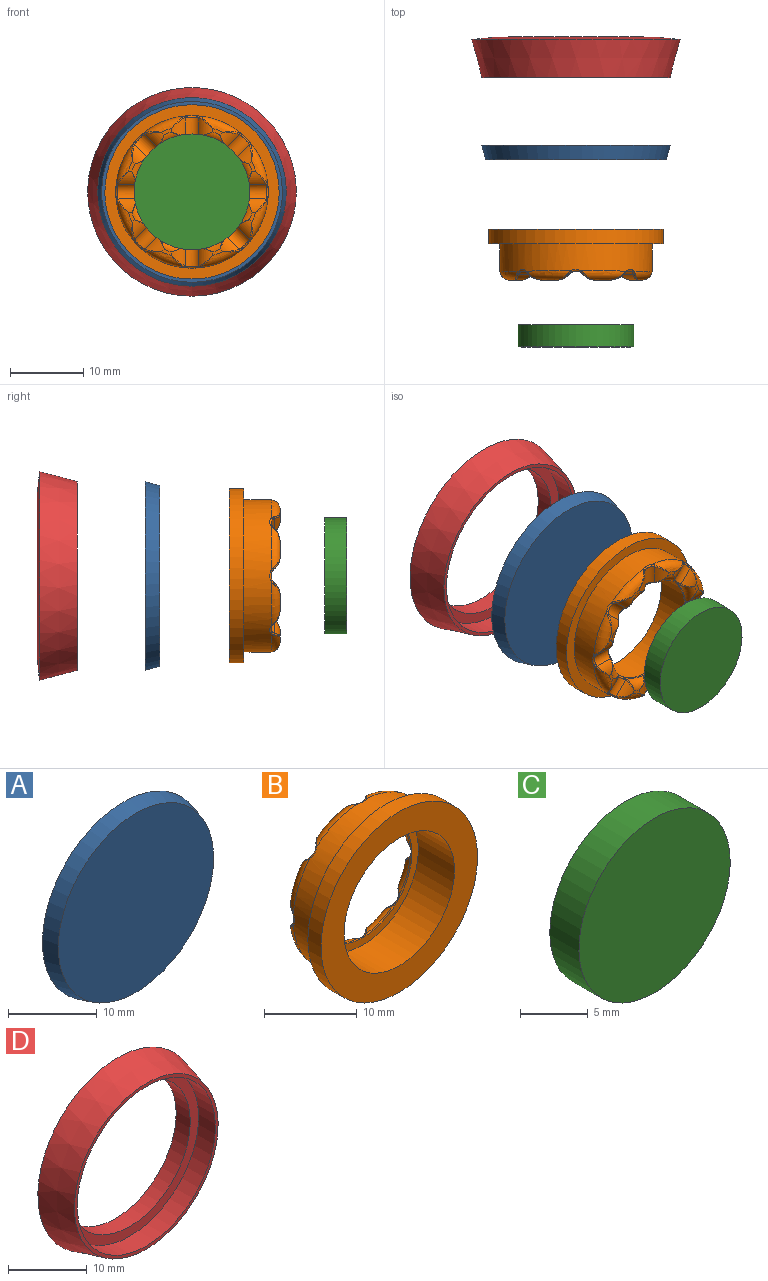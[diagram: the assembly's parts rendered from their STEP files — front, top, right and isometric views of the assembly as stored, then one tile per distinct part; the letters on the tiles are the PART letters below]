
ASSEMBLY  parts=4 mates=3
PART A: 3 faces, bbox 25.8x2x25.8 mm
  f0: plane 25.76x25.76mm, normal (0,1,0), area 521mm2, adj f1
  f1: cone r=12.35mm half-angle=14.9deg, axis (0,1,0), area 164mm2, adj f0,f2
  f2: plane 24.69x24.69mm, normal (0,-1,0), area 478.9mm2, adj f1
PART B: 135 faces, bbox 23.8x7x23.8 mm
  f0: plane 1.3x0.88mm, normal (0,1,0), area 0.6mm2, adj f3,f9,f49,f52
  f1: plane 1.3x0.88mm, normal (0,1,0), area 0.6mm2, adj f4,f10,f46,f51
  f2: plane 1.3x0.88mm, normal (0,1,0), area 0.6mm2, adj f5,f11,f33,f48
  f3: torus R=9.14mm, axis (0,-1,0), area 8.6mm2, adj f0,f29,f105,f106,f123,f124
  f4: torus R=9.14mm, axis (0,-1,0), area 8.6mm2, adj f1,f29,f95,f96,f108,f109
  f5: torus R=9.14mm, axis (0,-1,0), area 8.6mm2, adj f2,f29,f90,f91,f98,f99
  f6: torus R=9.14mm, axis (0,-1,0), area 8.6mm2, adj f15,f29,f80,f81,f93,f94
  f7: torus R=9.14mm, axis (0,-1,0), area 8.6mm2, adj f16,f29,f55,f56,f73,f74
  f8: torus R=9.14mm, axis (0,-1,0), area 8.6mm2, adj f29,f30,f70,f71,f83,f84
  f9: torus R=8.68mm, axis (0,-1,0), area 5.4mm2, adj f0,f23,f110,f111,f118,f119
  f10: torus R=8.68mm, axis (0,-1,0), area 5.4mm2, adj f1,f23,f100,f101,f113,f114
  f11: torus R=8.68mm, axis (0,-1,0), area 5.4mm2, adj f2,f23,f85,f86,f103,f104
  f12: torus R=8.68mm, axis (0,-1,0), area 5.4mm2, adj f15,f23,f75,f76,f88,f89
  f13: torus R=8.68mm, axis (0,-1,0), area 5.4mm2, adj f16,f23,f60,f61,f68,f69
  f14: torus R=8.68mm, axis (0,-1,0), area 5.4mm2, adj f23,f30,f65,f66,f78,f79
  f15: plane 1.3x0.88mm, normal (0,1,0), area 0.6mm2, adj f6,f12,f31,f43
  f16: plane 1.3x0.88mm, normal (0,1,0), area 0.6mm2, adj f7,f13,f38,f40
  f17: plane 1.3x0.88mm, normal (0,1,0), area 0.6mm2, adj f20,f22,f36,f41
  f18: plane 1.3x0.88mm, normal (0,1,0), area 0.6mm2, adj f19,f21,f34,f54
  f19: torus R=9.14mm, axis (0,-1,0), area 8.6mm2, adj f18,f29,f120,f121,f125,f126
  f20: torus R=9.14mm, axis (0,-1,0), area 8.6mm2, adj f17,f29,f58,f59,f128,f129
  f21: torus R=8.68mm, axis (0,-1,0), area 5.4mm2, adj f18,f23,f115,f116,f130,f131
  f22: torus R=8.68mm, axis (0,-1,0), area 5.4mm2, adj f17,f23,f63,f64,f133,f134
  f23: cylinder r=7.41mm len=14.83mm, axis (0,1,0), area 9.1mm2, adj f9,f10,f11,f12,f13,f14,f21,f22
  f24: plane 16.83x16.83mm, normal (0,-1,0), area 49.7mm2, adj f23,f25
  f25: cylinder r=8.41mm len=16.83mm, axis (0,1,0), area 290.8mm2, adj f24,f26
  f26: plane 23.83x23.83mm, normal (0,-1,0), area 223.5mm2, adj f25,f27
  f27: cylinder r=11.91mm len=23.83mm, axis (0,1,0), area 149.7mm2, adj f26,f28
  f28: plane 23.83x23.83mm, normal (0,1,0), area 105.2mm2, adj f27,f29
  f29: cylinder r=10.41mm len=20.83mm, axis (0,1,0), area 242.4mm2, adj f3,f4,f5,f6,f7,f8,f19,f20
  f30: plane 1.3x0.88mm, normal (0,1,0), area 0.6mm2, adj f8,f14,f37,f44
  f31: cylinder r=2.54mm len=2.53mm, axis (0,0,-1), area 3.5mm2, adj f15,f32,f89,f94
  f32: cylinder r=1.27mm len=2.61mm, axis (0,0,-1), area 5.5mm2, adj f31,f33,f86,f87,f88,f91,f92,f93
  f33: cylinder r=2.54mm len=2.53mm, axis (0,0,-1), area 3.5mm2, adj f2,f32,f85,f90
  f34: cylinder r=2.54mm len=2.53mm, axis (0,0,-1), area 3.5mm2, adj f18,f35,f125,f130
  f35: cylinder r=1.27mm len=2.61mm, axis (0,0,-1), area 5.5mm2, adj f34,f36,f126,f127,f128,f131,f132,f133
  f36: cylinder r=2.54mm len=2.53mm, axis (0,0,-1), area 3.5mm2, adj f17,f35,f129,f134
  f37: cylinder r=2.54mm len=2.53mm, axis (1,0,0), area 3.5mm2, adj f30,f39,f65,f70
  f38: cylinder r=2.54mm len=2.53mm, axis (1,0,0), area 3.5mm2, adj f16,f39,f69,f74
  f39: cylinder r=1.27mm len=2.61mm, axis (1,0,0), area 5.5mm2, adj f37,f38,f66,f67,f68,f71,f72,f73
  f40: cylinder r=2.54mm len=3.13mm, axis (0.71,0,0.71), area 3.5mm2, adj f16,f42,f55,f60
  f41: cylinder r=2.54mm len=3.13mm, axis (0.71,0,0.71), area 3.5mm2, adj f17,f42,f59,f64
  f42: cylinder r=1.27mm len=3.18mm, axis (0.71,0,0.71), area 5.5mm2, adj f40,f41,f56,f57,f58,f61,f62,f63
  f43: cylinder r=2.54mm len=3.13mm, axis (0.71,0,-0.71), area 3.5mm2, adj f15,f45,f75,f80
  f44: cylinder r=2.54mm len=3.13mm, axis (0.71,0,-0.71), area 3.5mm2, adj f30,f45,f79,f84
  f45: cylinder r=1.27mm len=3.18mm, axis (0.71,0,-0.71), area 5.5mm2, adj f43,f44,f76,f77,f78,f81,f82,f83
  f46: cylinder r=2.54mm len=3.13mm, axis (0.71,0,0.71), area 3.5mm2, adj f1,f47,f95,f100
  f47: cylinder r=1.27mm len=3.18mm, axis (0.71,0,0.71), area 5.5mm2, adj f46,f48,f96,f97,f98,f101,f102,f103
  f48: cylinder r=2.54mm len=3.13mm, axis (0.71,0,0.71), area 3.5mm2, adj f2,f47,f99,f104
  f49: cylinder r=2.54mm len=2.53mm, axis (1,0,0), area 3.5mm2, adj f0,f50,f105,f110
  f50: cylinder r=1.27mm len=2.61mm, axis (1,0,0), area 5.5mm2, adj f49,f51,f106,f107,f108,f111,f112,f113
  f51: cylinder r=2.54mm len=2.53mm, axis (1,0,0), area 3.5mm2, adj f1,f50,f109,f114
  f52: cylinder r=2.54mm len=3.13mm, axis (0.71,0,-0.71), area 3.5mm2, adj f0,f53,f119,f124
  f53: cylinder r=1.27mm len=3.18mm, axis (0.71,0,-0.71), area 5.5mm2, adj f52,f54,f116,f117,f118,f121,f122,f123
  f54: cylinder r=2.54mm len=3.13mm, axis (0.71,0,-0.71), area 3.5mm2, adj f18,f53,f115,f120
  f55: bspline ~2.65x1.19mm, area 0.4mm2, adj f7,f40,f56
  f56: bspline ~0.69x0.61mm, area 0.1mm2, adj f7,f42,f55,f57
  f57: bspline ~1.49x1.49mm, area 0.5mm2, adj f29,f42,f56,f58
  f58: bspline ~0.68x0.67mm, area 0.1mm2, adj f20,f42,f57,f59
  f59: bspline ~2.65x1.19mm, area 0.4mm2, adj f20,f41,f58
  f60: bspline ~2.1x1.27mm, area 0.2mm2, adj f13,f40,f61
  f61: bspline ~0.68x0.65mm, area 0.1mm2, adj f13,f42,f60,f62
  f62: bspline ~1.36x1.31mm, area 0.4mm2, adj f23,f42,f61,f63
  f63: bspline ~0.64x0.54mm, area 0.1mm2, adj f22,f42,f62,f64
  f64: bspline ~2.1x1.27mm, area 0.2mm2, adj f22,f41,f63
  f65: bspline ~2.14x1.27mm, area 0.3mm2, adj f14,f37,f66
  f66: bspline ~0.76x0.65mm, area 0.1mm2, adj f14,f39,f65,f67
  f67: bspline ~1.97x0.55mm, area 0.4mm2, adj f23,f39,f66,f68
  f68: bspline ~0.64x0.63mm, area 0.1mm2, adj f13,f39,f67,f69
  f69: bspline ~2.14x1.27mm, area 0.3mm2, adj f13,f38,f68
  f70: bspline ~2.08x1.69mm, area 0.4mm2, adj f8,f37,f71
  f71: bspline ~0.69x0.68mm, area 0.1mm2, adj f8,f39,f70,f72
  f72: bspline ~2.07x0.56mm, area 0.5mm2, adj f29,f39,f71,f73
  f73: bspline ~0.8x0.68mm, area 0.1mm2, adj f7,f39,f72,f74
  f74: bspline ~2.08x1.69mm, area 0.4mm2, adj f7,f38,f73
  f75: bspline ~2.1x1.27mm, area 0.2mm2, adj f12,f43,f76
  f76: bspline ~0.68x0.65mm, area 0.1mm2, adj f12,f45,f75,f77
  f77: bspline ~1.36x1.31mm, area 0.4mm2, adj f23,f45,f76,f78
  f78: bspline ~0.64x0.54mm, area 0.1mm2, adj f14,f45,f77,f79
  f79: bspline ~2.1x1.27mm, area 0.2mm2, adj f14,f44,f78
  f80: bspline ~2.39x0.93mm, area 0.4mm2, adj f6,f43,f81
  f81: bspline ~0.69x0.61mm, area 0.1mm2, adj f6,f45,f80,f82
  f82: bspline ~1.49x1.49mm, area 0.5mm2, adj f29,f45,f81,f83
  f83: bspline ~0.68x0.67mm, area 0.1mm2, adj f8,f45,f82,f84
  f84: bspline ~2.65x1.19mm, area 0.4mm2, adj f8,f44,f83
  f85: bspline ~2.14x1.27mm, area 0.3mm2, adj f11,f33,f86
  f86: bspline ~0.76x0.65mm, area 0.1mm2, adj f11,f32,f85,f87
  f87: bspline ~1.97x0.55mm, area 0.4mm2, adj f23,f32,f86,f88
  f88: bspline ~0.64x0.63mm, area 0.1mm2, adj f12,f32,f87,f89
  f89: bspline ~2.14x1.27mm, area 0.3mm2, adj f12,f31,f88
  f90: bspline ~1.89x1.61mm, area 0.4mm2, adj f5,f33,f91
  f91: bspline ~0.69x0.68mm, area 0.1mm2, adj f5,f32,f90,f92
  f92: bspline ~1.87x0.56mm, area 0.5mm2, adj f29,f32,f91,f93
  f93: bspline ~0.8x0.68mm, area 0.1mm2, adj f6,f32,f92,f94
  f94: bspline ~1.89x1.61mm, area 0.4mm2, adj f6,f31,f93
  f95: bspline ~2.39x0.93mm, area 0.4mm2, adj f4,f46,f96
  f96: bspline ~0.69x0.61mm, area 0.1mm2, adj f4,f47,f95,f97
  f97: bspline ~1.49x1.49mm, area 0.5mm2, adj f29,f47,f96,f98
  f98: bspline ~0.68x0.67mm, area 0.1mm2, adj f5,f47,f97,f99
  f99: bspline ~2.65x1.19mm, area 0.4mm2, adj f5,f48,f98
  f100: bspline ~2.1x1.27mm, area 0.2mm2, adj f10,f46,f101
  f101: bspline ~0.68x0.65mm, area 0.1mm2, adj f10,f47,f100,f102
  f102: bspline ~1.36x1.31mm, area 0.4mm2, adj f23,f47,f101,f103
  f103: bspline ~0.64x0.54mm, area 0.1mm2, adj f11,f47,f102,f104
  f104: bspline ~2.1x1.27mm, area 0.2mm2, adj f11,f48,f103
  f105: bspline ~2.08x1.69mm, area 0.4mm2, adj f3,f49,f106
  f106: bspline ~0.69x0.68mm, area 0.1mm2, adj f3,f50,f105,f107
  f107: bspline ~2.07x0.56mm, area 0.5mm2, adj f29,f50,f106,f108
  f108: bspline ~0.8x0.68mm, area 0.1mm2, adj f4,f50,f107,f109
  f109: bspline ~1.89x1.61mm, area 0.4mm2, adj f4,f51,f108
  f110: bspline ~2.14x1.27mm, area 0.3mm2, adj f9,f49,f111
  f111: bspline ~0.76x0.65mm, area 0.1mm2, adj f9,f50,f110,f112
  f112: bspline ~1.97x0.55mm, area 0.4mm2, adj f23,f50,f111,f113
  f113: bspline ~0.64x0.63mm, area 0.1mm2, adj f10,f50,f112,f114
  f114: bspline ~2.14x1.27mm, area 0.3mm2, adj f10,f51,f113
  f115: bspline ~2.1x1.27mm, area 0.2mm2, adj f21,f54,f116
  f116: bspline ~0.68x0.65mm, area 0.1mm2, adj f21,f53,f115,f117
  f117: bspline ~1.36x1.31mm, area 0.4mm2, adj f23,f53,f116,f118
  f118: bspline ~0.64x0.54mm, area 0.1mm2, adj f9,f53,f117,f119
  f119: bspline ~2.1x1.27mm, area 0.2mm2, adj f9,f52,f118
  f120: bspline ~2.65x1.19mm, area 0.4mm2, adj f19,f54,f121
  f121: bspline ~0.69x0.61mm, area 0.1mm2, adj f19,f53,f120,f122
  f122: bspline ~1.36x1.36mm, area 0.5mm2, adj f29,f53,f121,f123
  f123: bspline ~0.68x0.67mm, area 0.1mm2, adj f3,f53,f122,f124
  f124: bspline ~2.65x1.19mm, area 0.4mm2, adj f3,f52,f123
  f125: bspline ~2.08x1.69mm, area 0.4mm2, adj f19,f34,f126
  f126: bspline ~0.8x0.68mm, area 0.1mm2, adj f19,f35,f125,f127
  f127: bspline ~1.87x0.56mm, area 0.5mm2, adj f29,f35,f126,f128
  f128: bspline ~0.69x0.68mm, area 0.1mm2, adj f20,f35,f127,f129
  f129: bspline ~1.89x1.61mm, area 0.4mm2, adj f20,f36,f128
  f130: bspline ~2.14x1.27mm, area 0.3mm2, adj f21,f34,f131
  f131: bspline ~0.64x0.63mm, area 0.1mm2, adj f21,f35,f130,f132
  f132: bspline ~1.97x0.55mm, area 0.4mm2, adj f23,f35,f131,f133
  f133: bspline ~0.76x0.65mm, area 0.1mm2, adj f22,f35,f132,f134
  f134: bspline ~2.14x1.27mm, area 0.3mm2, adj f22,f36,f133
PART C: 3 faces, bbox 15.8x3x15.8 mm
  f0: cylinder r=7.92mm len=15.83mm, axis (0,-1,0), area 151.6mm2, adj f1,f2
  f1: plane 15.83x15.83mm, normal (0,1,0), area 196.8mm2, adj f0
  f2: plane 15.83x15.83mm, normal (0,-1,0), area 196.8mm2, adj f0
PART D: 6 faces, bbox 28.5x5.5x28.5 mm
  f0: cone r=14.25mm half-angle=14.9deg, axis (0,1,0), area 456.7mm2, adj f1,f2
  f1: sphere r=124.14mm, area 267.8mm2, adj f0,f5
  f2: plane 25.75x25.75mm, normal (0,-1,0), area 39.7mm2, adj f0,f3
  f3: cylinder r=12.37mm len=24.75mm, axis (0,-1,0), area 233.3mm2, adj f2,f4
  f4: plane 24.75x24.75mm, normal (0,-1,0), area 109.6mm2, adj f3,f5
  f5: cylinder r=10.87mm len=21.75mm, axis (0,-1,0), area 172.4mm2, adj f1,f4
PLACE A t=(16.99,3.95,-16.6)mm
PLACE B rot(axis=(-0.71,0,0.71),180deg) t=(16.99,-9.53,-27.02)mm
PLACE C t=(16.99,-23.62,-16.6)mm
PLACE D t=(16.99,13.2,-16.6)mm
MATE cylindrical D.f0 <-> A.f1  axis (0,-1,0) through (16.99,18.72,-16.6)mm
MATE cylindrical C.f0 <-> B.f3  axis (0,-1,0) through (16.99,-22.1,-16.6)mm
MATE cylindrical B.f23 <-> D.f0  axis (0,-1,0) through (16.99,-7.53,-16.6)mm
